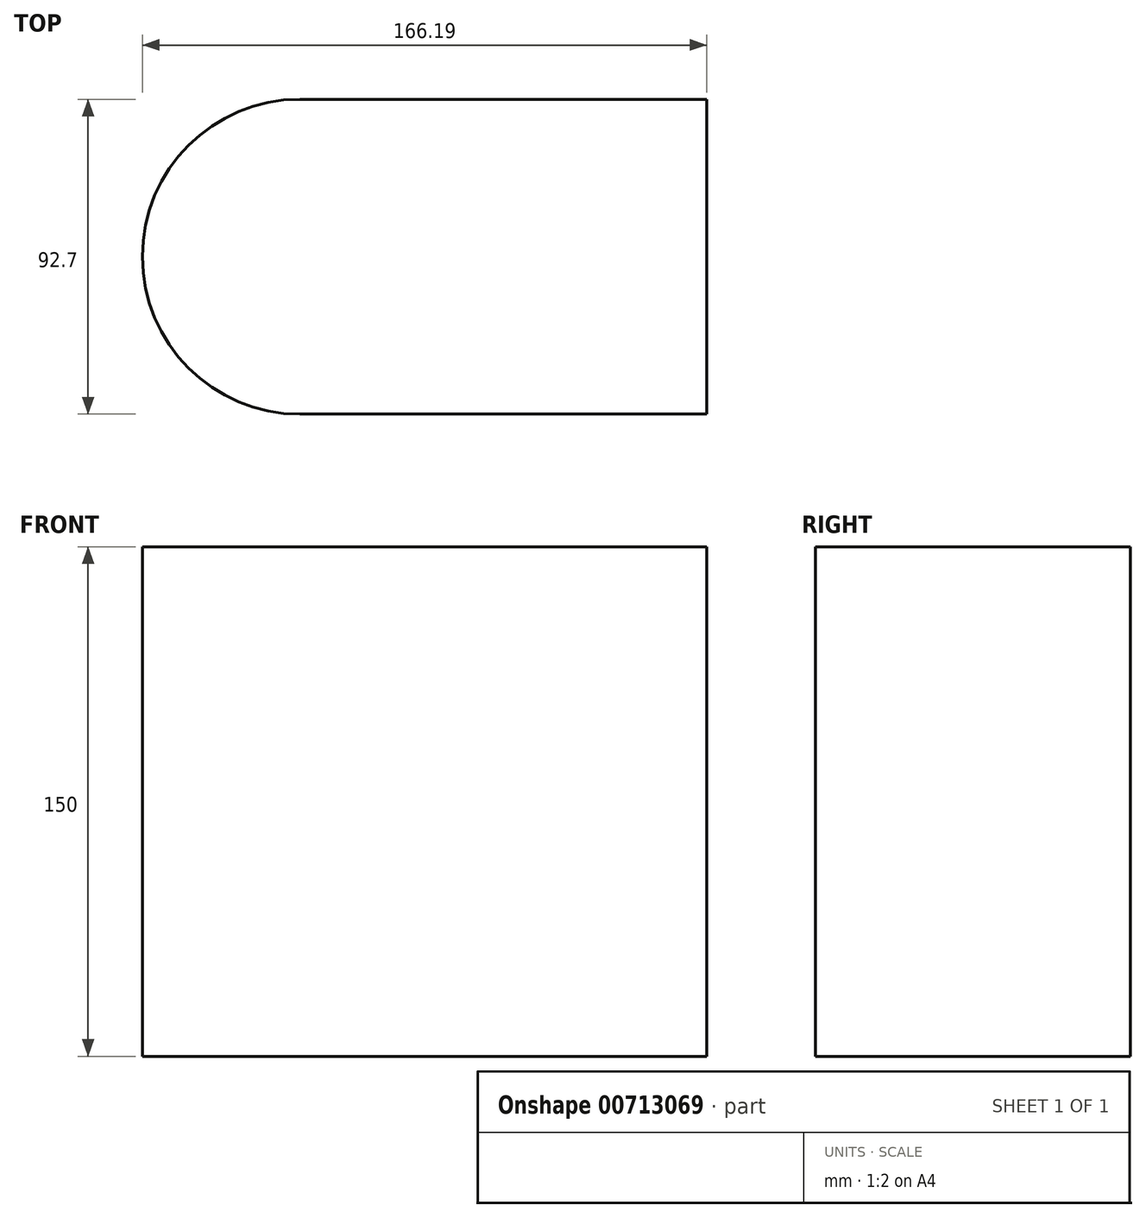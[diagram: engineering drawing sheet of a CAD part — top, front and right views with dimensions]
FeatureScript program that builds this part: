
annotation { "Feature Type Name" : "Feature", "Feature Type Description" : "" }
export const myFeature = defineFeature(function(context is Context, id is Id, definition is map)
    precondition{}
    {
        {
            var Q0;
            Q0=qCreatedBy(makeId("Top.planeOp"),FACE);
            var sketch = newSketch(context, id + "F0", { "sketchPlane" : qUnion([Q0])});
            skLineSegment(sketch, "E0.bottom", {"start": v(-46.62, 50.47) * mm, "end": v(73.23, 50.47) * mm});
            skLineSegment(sketch, "E0.top", {"start": v(-46.62, -42.23) * mm, "end": v(73.23, -42.23) * mm});
            skLineSegment(sketch, "E0.left", {"start": v(-46.62, 50.47) * mm, "end": v(-46.62, -42.23) * mm});
            skLineSegment(sketch, "E0.right", {"start": v(73.23, 50.47) * mm, "end": v(73.23, -42.23) * mm});
            skArc(sketch, "E1", {"start": v(-46.62, -42.23) * mm, "mid": v(-92.96, 4.12) * mm, "end": v(-46.62, 50.47) * mm});
            skSolve(sketch);
        }
        {
            var Q0;
            Q0=makeQuery(id+"F0.imprint","IMPRINT",FACE,{"disambiguationData":[TD([[makeQuery(id+"F0.imprint","IMPRINT",EDGE,{"derivedFrom":sQuery(id+"F0.wireOp",EDGE,"E0.bottom")}),-1.0]])]});
            var Q1;
            Q1=makeQuery(id+"F0.imprint","IMPRINT",FACE,{"disambiguationData":[TD([[makeQuery(id+"F0.imprint","IMPRINT",EDGE,{"derivedFrom":sQuery(id+"F0.wireOp",EDGE,"E0.left")}),-1.0]])]});
            extrude(context, id + "F1", {"entities" : qUnion([Q0, Q1]), "depth" : 150 * mm, "offsetDistance" : 25.4 * mm});
        }
    });
